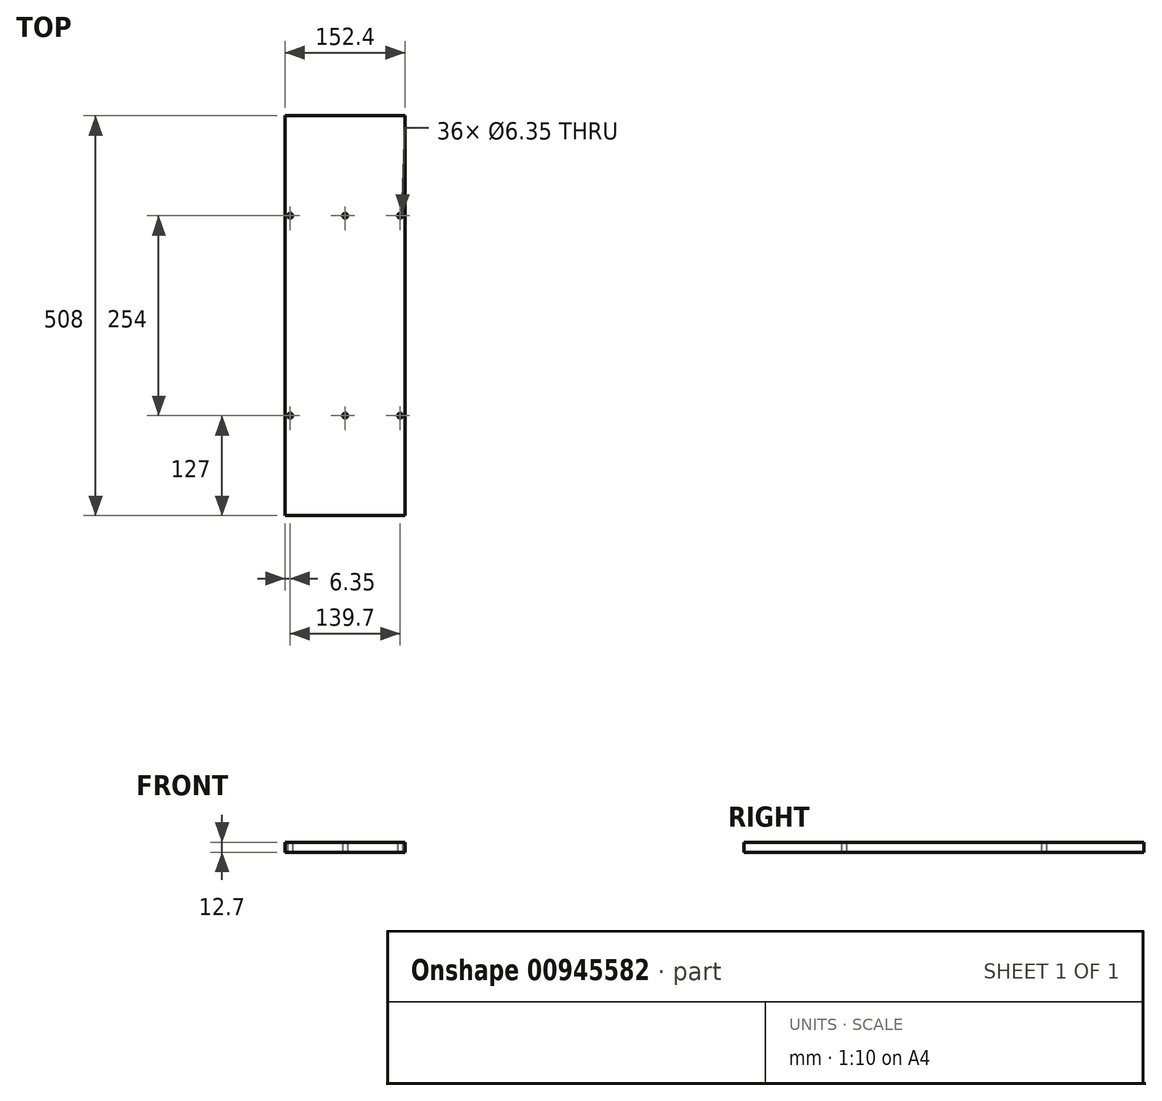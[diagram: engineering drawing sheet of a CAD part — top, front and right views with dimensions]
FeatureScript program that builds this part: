
annotation { "Feature Type Name" : "Feature", "Feature Type Description" : "" }
export const myFeature = defineFeature(function(context is Context, id is Id, definition is map)
    precondition{}
    {
        {
            var Q0;
            Q0=qCreatedBy(makeId("Top.planeOp"),FACE);
            var sketch = newSketch(context, id + "F0", { "sketchPlane" : qUnion([Q0])});
            skLineSegment(sketch, "E0.bottom", {"start": v(76.2, -254) * mm, "end": v(-76.2, -254) * mm});
            skLineSegment(sketch, "E0.top", {"start": v(76.2, 254) * mm, "end": v(-76.2, 254) * mm});
            skLineSegment(sketch, "E0.left", {"start": v(76.2, -254) * mm, "end": v(76.2, 254) * mm});
            skLineSegment(sketch, "E0.right", {"start": v(-76.2, -254) * mm, "end": v(-76.2, 254) * mm});
            skPoint(sketch, "E0.middle", {"position": v(0, 0) * mm});
            skSolve(sketch);
        }
        {
            var Q0;
            Q0=qCreatedBy(makeId("Top.planeOp"),FACE);
            var sketch = newSketch(context, id + "F1", { "sketchPlane" : qUnion([Q0])});
            skLineSegment(sketch, "E1", {"start": v(0, 254) * mm, "end": v(0, 127) * mm, "construction": true});
            skLineSegment(sketch, "E2", {"start": v(0, 127) * mm, "end": v(0, 0) * mm, "construction": true});
            skLineSegment(sketch, "E3", {"start": v(0, 0) * mm, "end": v(0, -127) * mm, "construction": true});
            skLineSegment(sketch, "E4", {"start": v(0, -127) * mm, "end": v(0, -254) * mm, "construction": true});
            skCircle(sketch, "E5", {"center": v(-69.85, 127) * mm, "radius": 3.18 * mm});
            skCircle(sketch, "E6", {"center": v(69.85, 127) * mm, "radius": 3.18 * mm});
            skCircle(sketch, "E7", {"center": v(69.85, -127) * mm, "radius": 3.18 * mm});
            skCircle(sketch, "E8", {"center": v(-69.85, -127) * mm, "radius": 3.18 * mm});
            skCircle(sketch, "E9", {"center": v(0, 127) * mm, "radius": 3.18 * mm});
            skCircle(sketch, "E10", {"center": v(0, -127) * mm, "radius": 3.18 * mm});
            skSolve(sketch);
        }
        {
            var Q0;
            Q0=qSketchRegion(id+"F0",true);
            extrude(context, id + "F2", {"entities" : qUnion([Q0]), "depth" : 12.7 * mm, "offsetDistance" : 25 * mm});
        }
        {
            var Q0;
            Q0=qSketchRegion(id+"F1",true);
            var Q1;
            Q1=makeQuery(id+"F2.opExtrude","CAP_FACE",FACE,{"disambiguationData":[OSD([sQuery(id+"F0.wireOp",EDGE,"E0.bottom"),sQuery(id+"F0.wireOp",EDGE,"E0.top"),sQuery(id+"F0.wireOp",EDGE,"E0.left"),sQuery(id+"F0.wireOp",EDGE,"E0.right")])],"isStart":false});
            extrude(context, id + "F3", {"entities" : qUnion([Q0]), "operationType" : NewBodyOperationType.REMOVE, "endBound" : BoundingType.UP_TO_SURFACE, "depth" : 25 * mm, "endBoundEntityFace" : qUnion([Q1]), "offsetDistance" : 25 * mm});
        }
    });
